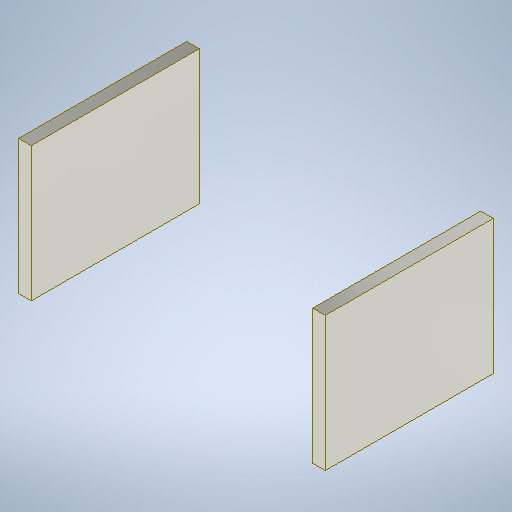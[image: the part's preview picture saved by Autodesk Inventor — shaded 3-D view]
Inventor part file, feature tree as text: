
AUTODESK INVENTOR PART (.ipt)
format: ipt  version: 2025.1 (Build 291241000, 241)  size: 216,064 bytes
history: native  units: mm
features: extrude x1, sketch x1
ambient origin geometry x8: Origin, YZ Plane, XZ Plane, XY Plane, X Axis, Y Axis, Z Axis, Center Point
bodies: Solid1 (feature_tree)
feature tree (2):
  extrude  "Extrusion1"  Depth=3.0mm
  sketch  "Sketch1"  dims[d0=73.0mm d1=3.0mm d2=32.0mm d3=16.0mm d5=0.0mm]
